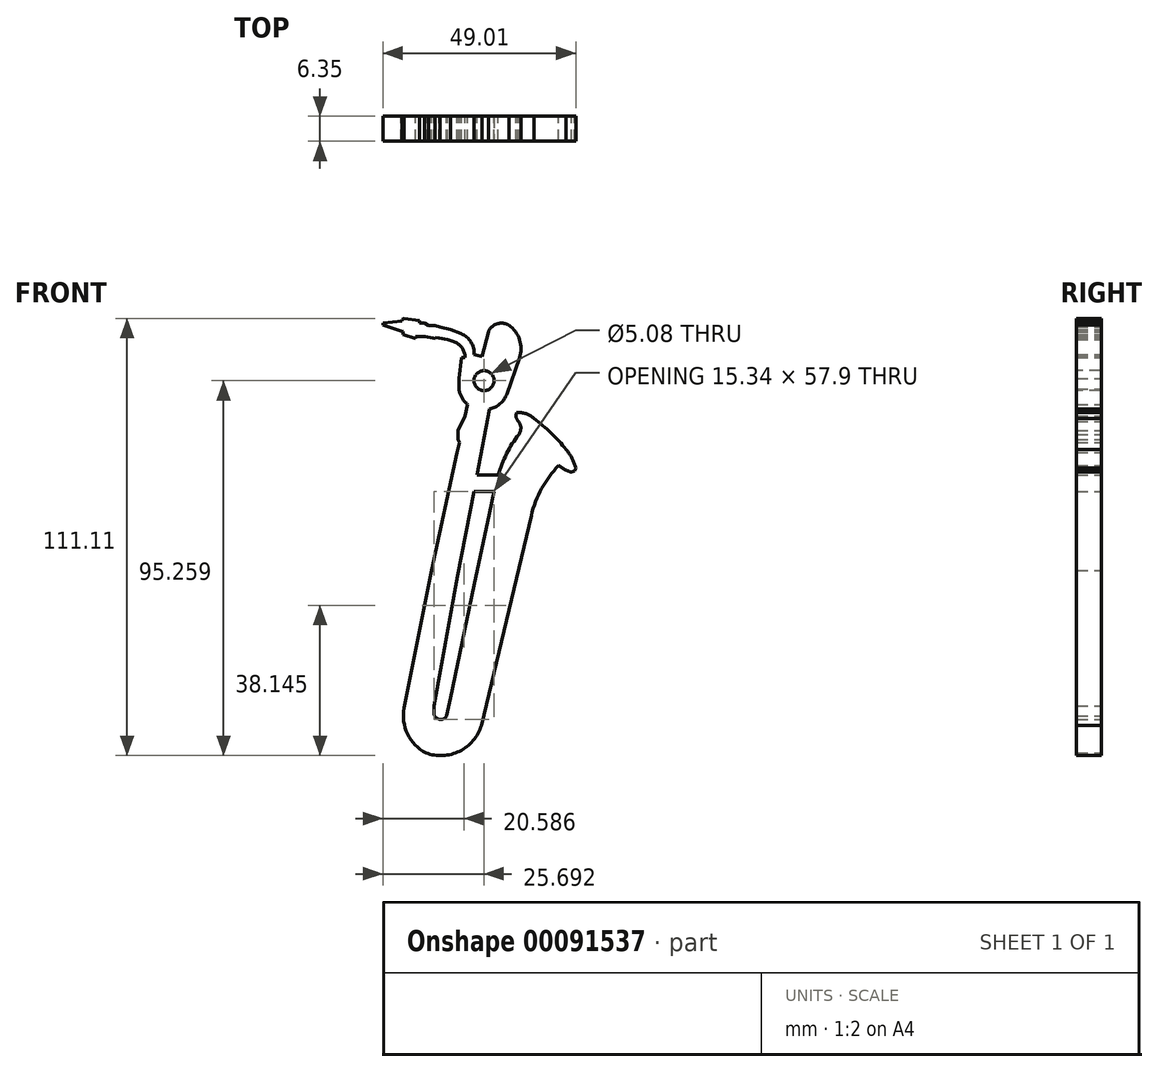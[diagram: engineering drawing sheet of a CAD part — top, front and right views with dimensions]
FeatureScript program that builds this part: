
annotation { "Feature Type Name" : "Feature", "Feature Type Description" : "" }
export const myFeature = defineFeature(function(context is Context, id is Id, definition is map)
    precondition{}
    {
        {
            var Q0;
            Q0=qCreatedBy(makeId("Front.planeOp"),FACE);
            var sketch = newSketch(context, id + "F0", { "sketchPlane" : qUnion([Q0])});
            skLineSegment(sketch, "E0", {"start": v(-16.27, 59.07) * mm, "end": v(-20.89, 60.53) * mm});
            skLineSegment(sketch, "E1", {"start": v(-20.89, 60.53) * mm, "end": v(-20.89, 61.15) * mm});
            skLineSegment(sketch, "E2", {"start": v(-20.89, 61.15) * mm, "end": v(-16.02, 61.61) * mm});
            skLineSegment(sketch, "E3", {"start": v(-16.02, 61.61) * mm, "end": v(-16.06, 62) * mm});
            skLineSegment(sketch, "E4", {"start": v(-16.06, 62) * mm, "end": v(-15.55, 62.3) * mm});
            skLineSegment(sketch, "E5", {"start": v(-15.55, 62.3) * mm, "end": v(-11.6, 61.66) * mm});
            skLineSegment(sketch, "E6", {"start": v(-11.6, 61.66) * mm, "end": v(-11.6, 61.14) * mm});
            skLineSegment(sketch, "E7", {"start": v(-11.6, 61.14) * mm, "end": v(-10.33, 61.14) * mm});
            skLineSegment(sketch, "E8", {"start": v(-10.33, 61.14) * mm, "end": v(-9.35, 60.46) * mm});
            skLineSegment(sketch, "E9", {"start": v(-9.35, 60.46) * mm, "end": v(-7.64, 60.46) * mm});
            skLineSegment(sketch, "E10", {"start": v(-7.64, 60.46) * mm, "end": v(-6.34, 60.05) * mm});
            skLineSegment(sketch, "E11", {"start": v(-6.34, 60.05) * mm, "end": v(-3.75, 59.45) * mm});
            skLineSegment(sketch, "E12", {"start": v(-3.75, 59.45) * mm, "end": v(-1.04, 58.37) * mm});
            skArc(sketch, "E13", {"start": v(2.28, 53.12) * mm, "mid": v(1.47, 56.28) * mm, "end": v(-1.04, 58.37) * mm});
            skLineSegment(sketch, "E14", {"start": v(-16.27, 59.07) * mm, "end": v(-15.83, 58.89) * mm});
            skLineSegment(sketch, "E15", {"start": v(-15.83, 58.89) * mm, "end": v(-15.83, 58.2) * mm});
            skLineSegment(sketch, "E16", {"start": v(-15.83, 58.2) * mm, "end": v(-12.62, 57.18) * mm});
            skLineSegment(sketch, "E17", {"start": v(-12.62, 57.18) * mm, "end": v(-12.62, 57.67) * mm});
            skLineSegment(sketch, "E18", {"start": v(-12.62, 57.67) * mm, "end": v(-10.24, 57.67) * mm});
            skLineSegment(sketch, "E19", {"start": v(-10.24, 57.67) * mm, "end": v(-7.58, 57.14) * mm});
            skLineSegment(sketch, "E20", {"start": v(-7.58, 57.14) * mm, "end": v(-7.58, 57.43) * mm});
            skLineSegment(sketch, "E21", {"start": v(-7.58, 57.43) * mm, "end": v(-6.64, 57.32) * mm});
            skLineSegment(sketch, "E22", {"start": v(-6.64, 57.32) * mm, "end": v(-4.5, 56.95) * mm});
            skLineSegment(sketch, "E23", {"start": v(-4.5, 56.95) * mm, "end": v(-2.95, 56.4) * mm});
            skArc(sketch, "E24", {"start": v(0, 52.38) * mm, "mid": v(-0.85, 54.85) * mm, "end": v(-2.95, 56.4) * mm});
            skLineSegment(sketch, "E25", {"start": v(0, 52.38) * mm, "end": v(-0.88, 52.38) * mm});
            skLineSegment(sketch, "E26", {"start": v(-0.88, 52.38) * mm, "end": v(-1.57, 46.96) * mm});
            skLineSegment(sketch, "E27", {"start": v(-1.57, 46.96) * mm, "end": v(-1.57, 44.26) * mm});
            skArc(sketch, "E28", {"start": v(-1.57, 44.26) * mm, "mid": v(-0.85, 42.11) * mm, "end": v(0.64, 40.4) * mm});
            skLineSegment(sketch, "E29", {"start": v(0.64, 40.4) * mm, "end": v(0, 37.46) * mm});
            skLineSegment(sketch, "E30", {"start": v(0, 37.46) * mm, "end": v(-1.84, 33.77) * mm});
            skLineSegment(sketch, "E31", {"start": v(-1.84, 33.77) * mm, "end": v(-1.84, 31.5) * mm});
            skLineSegment(sketch, "E32", {"start": v(-1.84, 31.5) * mm, "end": v(-1.42, 30.8) * mm});
            skLineSegment(sketch, "E33", {"start": v(-1.42, 30.8) * mm, "end": v(-2.08, 28.24) * mm});
            skLineSegment(sketch, "E34", {"start": v(-2.08, 28.24) * mm, "end": v(-8.53, -1.82) * mm});
            skLineSegment(sketch, "E35", {"start": v(-8.53, -1.82) * mm, "end": v(-15.49, -36.68) * mm});
            skArc(sketch, "E36", {"start": v(-15.49, -36.68) * mm, "mid": v(-14.65, -43.33) * mm, "end": v(-9.98, -48.14) * mm});
            skArc(sketch, "E37", {"start": v(-9.98, -48.14) * mm, "mid": v(-1.43, -47.7) * mm, "end": v(4.11, -41.18) * mm});
            skLineSegment(sketch, "E38", {"start": v(4.11, -41.18) * mm, "end": v(16.8, 12.22) * mm});
            skArc(sketch, "E39", {"start": v(23.77, 24.92) * mm, "mid": v(19.43, 19.04) * mm, "end": v(16.8, 12.22) * mm});
            skArc(sketch, "E40", {"start": v(23.77, 24.92) * mm, "mid": v(25.3, 23.91) * mm, "end": v(26.98, 23.2) * mm});
            skLineSegment(sketch, "E41", {"start": v(26.98, 23.2) * mm, "end": v(27.74, 23.46) * mm});
            skLineSegment(sketch, "E42", {"start": v(27.74, 23.46) * mm, "end": v(28.12, 24.23) * mm});
            skArc(sketch, "E43", {"start": v(28.12, 24.23) * mm, "mid": v(27.16, 26.7) * mm, "end": v(25.68, 28.9) * mm});
            skArc(sketch, "E44", {"start": v(25.68, 28.9) * mm, "mid": v(21.83, 33.14) * mm, "end": v(17.45, 36.84) * mm});
            skArc(sketch, "E45", {"start": v(17.45, 36.84) * mm, "mid": v(15.43, 38.06) * mm, "end": v(13.09, 38.34) * mm});
            skArc(sketch, "E46", {"start": v(13.09, 38.34) * mm, "mid": v(12.98, 37.14) * mm, "end": v(13.57, 36.1) * mm});
            skArc(sketch, "E47", {"start": v(13.63, 32.82) * mm, "mid": v(14.15, 34.47) * mm, "end": v(13.57, 36.1) * mm});
            skLineSegment(sketch, "E48", {"start": v(6.18, 12.8) * mm, "end": v(2.24, -5.56) * mm});
            skLineSegment(sketch, "E49", {"start": v(2.24, -5.56) * mm, "end": v(-3.73, -34.17) * mm});
            skLineSegment(sketch, "E50", {"start": v(-3.73, -34.17) * mm, "end": v(-4.69, -38.75) * mm});
            skArc(sketch, "E51", {"start": v(-7.97, -37.88) * mm, "mid": v(-6.66, -39.57) * mm, "end": v(-4.69, -38.75) * mm});
            skLineSegment(sketch, "E52", {"start": v(-7.97, -37.88) * mm, "end": v(-7.97, -36.22) * mm});
            skLineSegment(sketch, "E53", {"start": v(-7.97, -36.22) * mm, "end": v(-1.88, -3.11) * mm});
            skArc(sketch, "E54", {"start": v(6.2, 39.25) * mm, "mid": v(8.92, 40.6) * mm, "end": v(10.62, 43.11) * mm});
            skLineSegment(sketch, "E55", {"start": v(10.62, 43.11) * mm, "end": v(13.77, 52.24) * mm});
            skArc(sketch, "E56", {"start": v(13.77, 52.24) * mm, "mid": v(13.82, 56.83) * mm, "end": v(11.1, 60.52) * mm});
            skArc(sketch, "E57", {"start": v(11.1, 60.52) * mm, "mid": v(8.08, 60.87) * mm, "end": v(5.89, 58.77) * mm});
            skLineSegment(sketch, "E58", {"start": v(5.89, 58.77) * mm, "end": v(4.22, 52.52) * mm});
            skLineSegment(sketch, "E59", {"start": v(4.22, 52.52) * mm, "end": v(2.28, 53.12) * mm});
            skLineSegment(sketch, "E60", {"start": v(-1.88, -3.11) * mm, "end": v(2.24, 18.28) * mm});
            skLineSegment(sketch, "E61", {"start": v(6.18, 12.8) * mm, "end": v(7.36, 18.28) * mm});
            skLineSegment(sketch, "E62", {"start": v(7.36, 18.28) * mm, "end": v(2.24, 18.28) * mm});
            skLineSegment(sketch, "E63", {"start": v(6.2, 39.25) * mm, "end": v(2.96, 22.46) * mm});
            skLineSegment(sketch, "E64", {"start": v(2.96, 22.46) * mm, "end": v(8.4, 22.46) * mm});
            skArc(sketch, "E65", {"start": v(13.63, 32.82) * mm, "mid": v(10.52, 27.9) * mm, "end": v(8.4, 22.46) * mm});
            skSolve(sketch);
        }
        {
            var Q0;
            Q0=makeQuery(id+"F0.imprint","IMPRINT",FACE,{"disambiguationData":[TD([[makeQuery(id+"F0.imprint","IMPRINT",EDGE,{"derivedFrom":sQuery(id+"F0.wireOp",EDGE,"E0")}),-1.0]])]});
            extrude(context, id + "F1", {"entities" : qUnion([Q0]), "depth" : 6.35 * mm});
        }
        {
            var Q0;
            Q0=makeQuery(id+"F1.opExtrude","CAP_FACE",FACE,{"disambiguationData":[OSD([sQuery(id+"F0.wireOp",EDGE,"E0"),sQuery(id+"F0.wireOp",EDGE,"E1"),sQuery(id+"F0.wireOp",EDGE,"E2"),sQuery(id+"F0.wireOp",EDGE,"E3"),sQuery(id+"F0.wireOp",EDGE,"E4"),sQuery(id+"F0.wireOp",EDGE,"E5"),sQuery(id+"F0.wireOp",EDGE,"E6"),sQuery(id+"F0.wireOp",EDGE,"E7"),sQuery(id+"F0.wireOp",EDGE,"E8"),sQuery(id+"F0.wireOp",EDGE,"E9"),sQuery(id+"F0.wireOp",EDGE,"E10"),sQuery(id+"F0.wireOp",EDGE,"E11"),sQuery(id+"F0.wireOp",EDGE,"E12"),sQuery(id+"F0.wireOp",EDGE,"E13"),sQuery(id+"F0.wireOp",EDGE,"E14"),sQuery(id+"F0.wireOp",EDGE,"E15"),sQuery(id+"F0.wireOp",EDGE,"E16"),sQuery(id+"F0.wireOp",EDGE,"E17"),sQuery(id+"F0.wireOp",EDGE,"E18"),sQuery(id+"F0.wireOp",EDGE,"E19"),sQuery(id+"F0.wireOp",EDGE,"E20"),sQuery(id+"F0.wireOp",EDGE,"E21"),sQuery(id+"F0.wireOp",EDGE,"E22"),sQuery(id+"F0.wireOp",EDGE,"E23"),sQuery(id+"F0.wireOp",EDGE,"E24"),sQuery(id+"F0.wireOp",EDGE,"E25"),sQuery(id+"F0.wireOp",EDGE,"E26"),sQuery(id+"F0.wireOp",EDGE,"E27"),sQuery(id+"F0.wireOp",EDGE,"E28"),sQuery(id+"F0.wireOp",EDGE,"E29"),sQuery(id+"F0.wireOp",EDGE,"E30"),sQuery(id+"F0.wireOp",EDGE,"E31"),sQuery(id+"F0.wireOp",EDGE,"E32"),sQuery(id+"F0.wireOp",EDGE,"E33"),sQuery(id+"F0.wireOp",EDGE,"E34"),sQuery(id+"F0.wireOp",EDGE,"E35"),sQuery(id+"F0.wireOp",EDGE,"E36"),sQuery(id+"F0.wireOp",EDGE,"E37"),sQuery(id+"F0.wireOp",EDGE,"E38"),sQuery(id+"F0.wireOp",EDGE,"E39"),sQuery(id+"F0.wireOp",EDGE,"E40"),sQuery(id+"F0.wireOp",EDGE,"E41"),sQuery(id+"F0.wireOp",EDGE,"E42"),sQuery(id+"F0.wireOp",EDGE,"E43"),sQuery(id+"F0.wireOp",EDGE,"E44"),sQuery(id+"F0.wireOp",EDGE,"E45"),sQuery(id+"F0.wireOp",EDGE,"E46"),sQuery(id+"F0.wireOp",EDGE,"E47"),sQuery(id+"F0.wireOp",EDGE,"E48"),sQuery(id+"F0.wireOp",EDGE,"E49"),sQuery(id+"F0.wireOp",EDGE,"E50"),sQuery(id+"F0.wireOp",EDGE,"E51"),sQuery(id+"F0.wireOp",EDGE,"E52"),sQuery(id+"F0.wireOp",EDGE,"E53"),sQuery(id+"F0.wireOp",EDGE,"E54"),sQuery(id+"F0.wireOp",EDGE,"E55"),sQuery(id+"F0.wireOp",EDGE,"E56"),sQuery(id+"F0.wireOp",EDGE,"E57"),sQuery(id+"F0.wireOp",EDGE,"E58"),sQuery(id+"F0.wireOp",EDGE,"E59"),sQuery(id+"F0.wireOp",EDGE,"E60"),sQuery(id+"F0.wireOp",EDGE,"E61"),sQuery(id+"F0.wireOp",EDGE,"E62"),sQuery(id+"F0.wireOp",EDGE,"E63"),sQuery(id+"F0.wireOp",EDGE,"E64"),sQuery(id+"F0.wireOp",EDGE,"E65")])],"isStart":false});
            var sketch = newSketch(context, id + "F2", { "sketchPlane" : qUnion([Q0])});
            skCircle(sketch, "E66", {"center": v(4.8, 46.44) * mm, "radius": 2.54 * mm});
            skLineSegment(sketch, "E67", {"start": v(0.64, 40.4) * mm, "end": v(4.8, 46.44) * mm, "construction": true});
            skLineSegment(sketch, "E68", {"start": v(0.64, 40.4) * mm, "end": v(6.2, 39.25) * mm, "construction": true});
            skSolve(sketch);
        }
        {
            var Q0;
            Q0=makeQuery(id+"F2.imprint","IMPRINT",FACE,{"disambiguationData":[TD([[makeQuery(id+"F2.imprint","IMPRINT",EDGE,{"derivedFrom":sQuery(id+"F2.wireOp",EDGE,"E66")}),1.0]])]});
            extrude(context, id + "F3", {"entities" : qUnion([Q0]), "operationType" : NewBodyOperationType.REMOVE, "oppositeDirection" : true, "depth" : 25.4 * mm});
        }
    });
